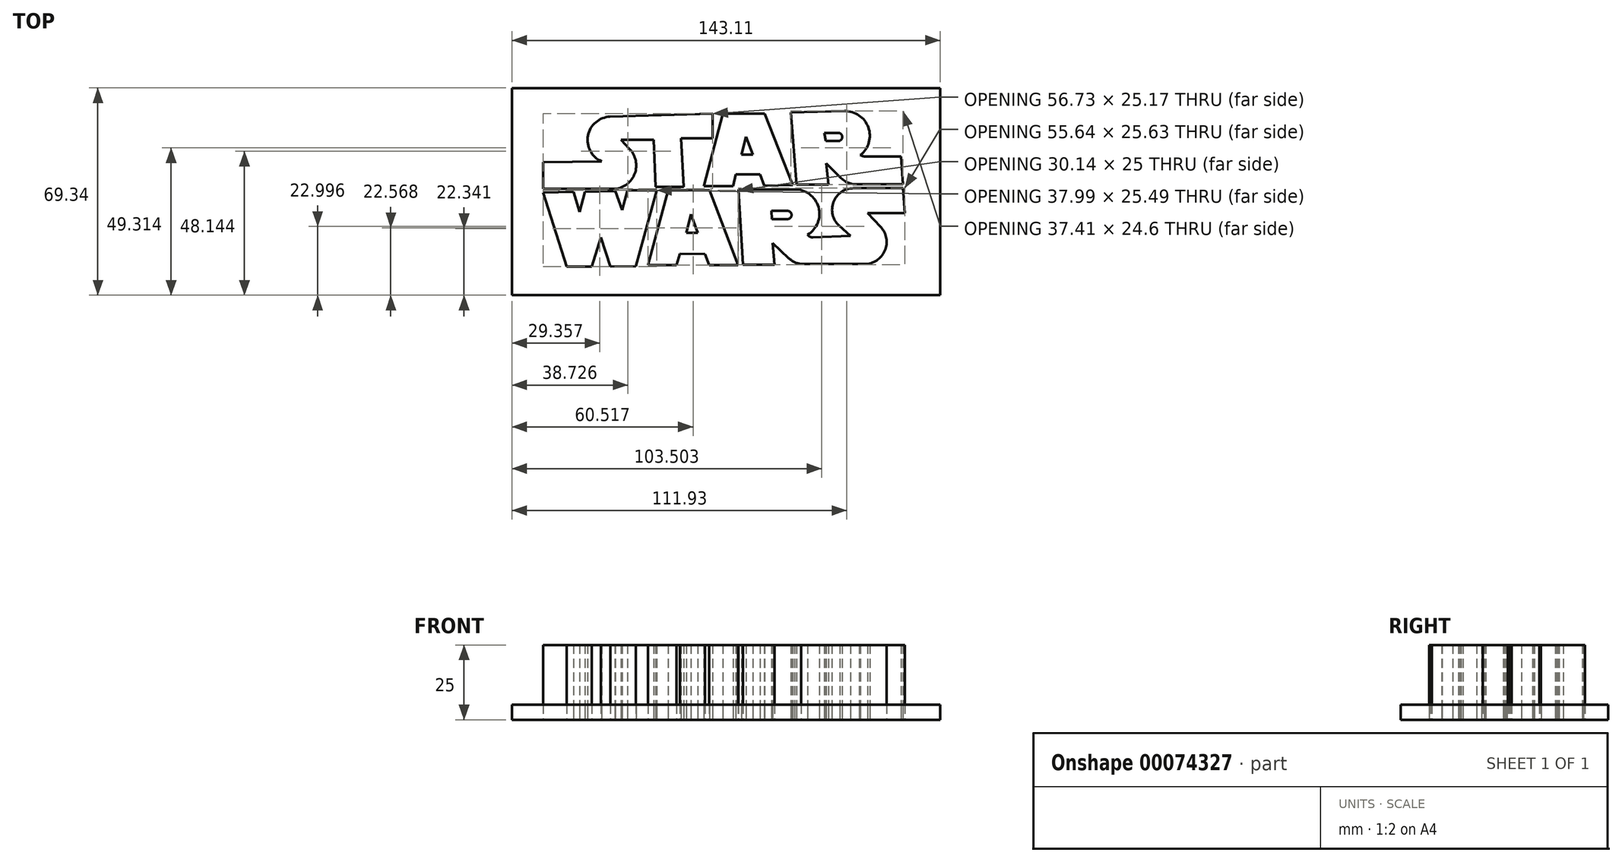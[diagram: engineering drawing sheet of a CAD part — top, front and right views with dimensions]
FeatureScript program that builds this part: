
annotation { "Feature Type Name" : "Feature", "Feature Type Description" : "" }
export const myFeature = defineFeature(function(context is Context, id is Id, definition is map)
    precondition{}
    {
        {
            var Q0;
            Q0=qCreatedBy(makeId("Top.planeOp"),FACE);
            var sketch = newSketch(context, id + "F0", { "sketchPlane" : qUnion([Q0])});
            skLineSegment(sketch, "E0", {"start": v(68.62, -36.54) * mm, "end": v(78.02, -36.54) * mm});
            skLineSegment(sketch, "E1", {"start": v(78.02, -36.54) * mm, "end": v(77.15, -20.37) * mm});
            skLineSegment(sketch, "E2", {"start": v(77.15, -20.37) * mm, "end": v(87.76, -20.37) * mm});
            skLineSegment(sketch, "E3", {"start": v(87.76, -20.37) * mm, "end": v(87.76, -12.11) * mm});
            skLineSegment(sketch, "E4", {"start": v(87.76, -12.11) * mm, "end": v(53.49, -13.1) * mm});
            skLineSegment(sketch, "E5", {"start": v(68.62, -36.54) * mm, "end": v(68.03, -20.87) * mm});
            skLineSegment(sketch, "E6", {"start": v(68.03, -20.87) * mm, "end": v(57.1, -20.87) * mm});
            skLineSegment(sketch, "E7", {"start": v(57.1, -20.87) * mm, "end": v(60.03, -23.97) * mm});
            skLineSegment(sketch, "E8", {"start": v(31.03, -28.3) * mm, "end": v(31.03, -37.28) * mm});
            skLineSegment(sketch, "E9", {"start": v(31.03, -37.28) * mm, "end": v(55.13, -37.28) * mm});
            skLineSegment(sketch, "E10", {"start": v(50.6, -28.05) * mm, "end": v(31.03, -28.3) * mm});
            skArc(sketch, "E11", {"start": v(53.49, -13.1) * mm, "mid": v(46.06, -19.42) * mm, "end": v(50.6, -28.05) * mm});
            skArc(sketch, "E12", {"start": v(55.13, -37.28) * mm, "mid": v(61.7, -32.14) * mm, "end": v(60.03, -23.97) * mm});
            skLineSegment(sketch, "E13", {"start": v(98.83, -19.8) * mm, "end": v(97.31, -25.8) * mm});
            skLineSegment(sketch, "E14", {"start": v(97.31, -25.8) * mm, "end": v(101.14, -25.8) * mm});
            skLineSegment(sketch, "E15", {"start": v(101.14, -25.8) * mm, "end": v(98.83, -19.8) * mm});
            skLineSegment(sketch, "E16", {"start": v(91.14, -12.01) * mm, "end": v(105.05, -12.01) * mm});
            skLineSegment(sketch, "E17", {"start": v(105.05, -12.01) * mm, "end": v(114.46, -35.91) * mm});
            skLineSegment(sketch, "E18", {"start": v(114.46, -35.91) * mm, "end": v(105.02, -36.2) * mm});
            skLineSegment(sketch, "E19", {"start": v(105.02, -36.2) * mm, "end": v(103.54, -32.45) * mm});
            skLineSegment(sketch, "E20", {"start": v(103.54, -32.45) * mm, "end": v(95.4, -32.45) * mm});
            skLineSegment(sketch, "E21", {"start": v(95.4, -32.45) * mm, "end": v(94.52, -36.4) * mm});
            skLineSegment(sketch, "E22", {"start": v(94.52, -36.4) * mm, "end": v(84.84, -36.4) * mm});
            skLineSegment(sketch, "E23", {"start": v(84.84, -36.4) * mm, "end": v(91.14, -12.01) * mm});
            skLineSegment(sketch, "E24.bottom", {"start": v(20.67, -3.5) * mm, "end": v(163.78, -3.5) * mm});
            skLineSegment(sketch, "E24.top", {"start": v(20.67, -72.84) * mm, "end": v(163.78, -72.84) * mm});
            skLineSegment(sketch, "E24.left", {"start": v(20.67, -3.5) * mm, "end": v(20.67, -72.84) * mm});
            skLineSegment(sketch, "E24.right", {"start": v(163.78, -3.5) * mm, "end": v(163.78, -72.84) * mm});
            skLineSegment(sketch, "E25", {"start": v(113.9, -11.65) * mm, "end": v(115.74, -35.83) * mm});
            skLineSegment(sketch, "E26", {"start": v(115.74, -35.83) * mm, "end": v(126.45, -35.83) * mm});
            skLineSegment(sketch, "E27", {"start": v(126.45, -35.83) * mm, "end": v(125.63, -28.76) * mm});
            skLineSegment(sketch, "E28", {"start": v(125.63, -28.76) * mm, "end": v(130.7, -33.69) * mm});
            skLineSegment(sketch, "E29", {"start": v(113.9, -11.65) * mm, "end": v(131.78, -11.23) * mm});
            skLineSegment(sketch, "E30", {"start": v(125.1, -18.49) * mm, "end": v(125.52, -21.17) * mm});
            skLineSegment(sketch, "E31", {"start": v(125.52, -21.17) * mm, "end": v(130.21, -21.17) * mm});
            skLineSegment(sketch, "E32", {"start": v(125.1, -18.49) * mm, "end": v(129.65, -18.49) * mm});
            skLineSegment(sketch, "E33", {"start": v(136.7, -35.68) * mm, "end": v(151.3, -35.68) * mm});
            skLineSegment(sketch, "E34", {"start": v(151.3, -35.68) * mm, "end": v(150.64, -26.43) * mm});
            skLineSegment(sketch, "E35", {"start": v(150.64, -26.43) * mm, "end": v(138.86, -26.43) * mm});
            skArc(sketch, "E36", {"start": v(130.7, -33.69) * mm, "mid": v(133.46, -35.37) * mm, "end": v(136.7, -35.68) * mm});
            skArc(sketch, "E37", {"start": v(137.16, -25.96) * mm, "mid": v(139.76, -16.66) * mm, "end": v(131.78, -11.23) * mm});
            skArc(sketch, "E38", {"start": v(137.16, -25.96) * mm, "mid": v(137.98, -26.3) * mm, "end": v(138.86, -26.43) * mm});
            skArc(sketch, "E39", {"start": v(130.21, -21.17) * mm, "mid": v(131.02, -19.6) * mm, "end": v(129.65, -18.49) * mm});
            skLineSegment(sketch, "E40", {"start": v(31.03, -38.52) * mm, "end": v(38.96, -63.2) * mm});
            skLineSegment(sketch, "E41", {"start": v(38.96, -63.2) * mm, "end": v(47.3, -63.2) * mm});
            skLineSegment(sketch, "E42", {"start": v(47.3, -63.2) * mm, "end": v(50.33, -53.49) * mm});
            skLineSegment(sketch, "E43", {"start": v(50.33, -53.49) * mm, "end": v(53.51, -63.24) * mm});
            skLineSegment(sketch, "E44", {"start": v(53.51, -63.24) * mm, "end": v(62.03, -63.09) * mm});
            skLineSegment(sketch, "E45", {"start": v(62.03, -63.09) * mm, "end": v(69.02, -37.76) * mm});
            skLineSegment(sketch, "E46", {"start": v(69.02, -37.76) * mm, "end": v(59.22, -37.76) * mm});
            skLineSegment(sketch, "E47", {"start": v(59.22, -37.76) * mm, "end": v(57.43, -44.37) * mm});
            skLineSegment(sketch, "E48", {"start": v(57.43, -44.37) * mm, "end": v(55.2, -37.98) * mm});
            skLineSegment(sketch, "E49", {"start": v(55.2, -37.98) * mm, "end": v(44.98, -38.18) * mm});
            skLineSegment(sketch, "E50", {"start": v(44.98, -38.18) * mm, "end": v(43.26, -44.9) * mm});
            skLineSegment(sketch, "E51", {"start": v(43.26, -44.9) * mm, "end": v(41.28, -38.29) * mm});
            skLineSegment(sketch, "E52", {"start": v(41.28, -38.29) * mm, "end": v(31.03, -38.52) * mm});
            skLineSegment(sketch, "E53", {"start": v(66.12, -62.77) * mm, "end": v(75.72, -62.77) * mm});
            skLineSegment(sketch, "E54", {"start": v(75.72, -62.77) * mm, "end": v(76.78, -58.98) * mm});
            skLineSegment(sketch, "E55", {"start": v(76.78, -58.98) * mm, "end": v(85.13, -59.05) * mm});
            skLineSegment(sketch, "E56", {"start": v(85.13, -59.05) * mm, "end": v(86.55, -62.73) * mm});
            skLineSegment(sketch, "E57", {"start": v(86.55, -62.73) * mm, "end": v(96.26, -62.74) * mm});
            skLineSegment(sketch, "E58", {"start": v(96.26, -62.74) * mm, "end": v(86.7, -37.77) * mm});
            skLineSegment(sketch, "E59", {"start": v(86.7, -37.77) * mm, "end": v(72.85, -37.77) * mm});
            skLineSegment(sketch, "E60", {"start": v(72.85, -37.77) * mm, "end": v(66.12, -62.77) * mm});
            skLineSegment(sketch, "E61", {"start": v(80.48, -45.71) * mm, "end": v(78.9, -51.96) * mm});
            skLineSegment(sketch, "E62", {"start": v(78.9, -51.96) * mm, "end": v(82.75, -51.96) * mm});
            skLineSegment(sketch, "E63", {"start": v(82.75, -51.96) * mm, "end": v(80.48, -45.71) * mm});
            skLineSegment(sketch, "E64", {"start": v(96.36, -37.45) * mm, "end": v(97.81, -62.66) * mm});
            skLineSegment(sketch, "E65", {"start": v(97.81, -62.66) * mm, "end": v(108.41, -62.66) * mm});
            skLineSegment(sketch, "E66", {"start": v(107.84, -55.43) * mm, "end": v(108.41, -62.66) * mm});
            skLineSegment(sketch, "E67", {"start": v(107.84, -55.43) * mm, "end": v(113.17, -60.43) * mm});
            skArc(sketch, "E68", {"start": v(113.17, -60.43) * mm, "mid": v(115.06, -61.73) * mm, "end": v(117.25, -62.41) * mm});
            skLineSegment(sketch, "E69", {"start": v(117.25, -62.41) * mm, "end": v(138.48, -62.41) * mm});
            skArc(sketch, "E70", {"start": v(138.48, -62.41) * mm, "mid": v(145.28, -57.94) * mm, "end": v(143.85, -49.93) * mm});
            skLineSegment(sketch, "E71", {"start": v(143.85, -49.93) * mm, "end": v(139.53, -45.38) * mm});
            skLineSegment(sketch, "E72", {"start": v(139.53, -45.38) * mm, "end": v(152, -45.38) * mm});
            skLineSegment(sketch, "E73", {"start": v(152, -45.38) * mm, "end": v(151.37, -37.03) * mm});
            skLineSegment(sketch, "E74", {"start": v(151.37, -37.03) * mm, "end": v(134.84, -37.03) * mm});
            skArc(sketch, "E75", {"start": v(134.84, -37.03) * mm, "mid": v(128.12, -41.66) * mm, "end": v(130.06, -49.6) * mm});
            skLineSegment(sketch, "E76", {"start": v(130.06, -49.6) * mm, "end": v(133.8, -52.93) * mm});
            skLineSegment(sketch, "E77", {"start": v(133.8, -52.93) * mm, "end": v(121.2, -53.48) * mm});
            skArc(sketch, "E78", {"start": v(119.48, -52.6) * mm, "mid": v(120.22, -53.27) * mm, "end": v(121.2, -53.48) * mm});
            skArc(sketch, "E79", {"start": v(119.48, -52.6) * mm, "mid": v(123.11, -43.37) * mm, "end": v(115.15, -37.43) * mm});
            skLineSegment(sketch, "E80", {"start": v(115.15, -37.43) * mm, "end": v(96.36, -37.45) * mm});
            skLineSegment(sketch, "E81", {"start": v(107.37, -44.62) * mm, "end": v(107.53, -47.35) * mm});
            skLineSegment(sketch, "E82", {"start": v(107.53, -47.35) * mm, "end": v(112.73, -47.35) * mm});
            skLineSegment(sketch, "E83", {"start": v(107.37, -44.62) * mm, "end": v(112.73, -44.62) * mm});
            skArc(sketch, "E84", {"start": v(112.73, -47.35) * mm, "mid": v(114.1, -45.98) * mm, "end": v(112.73, -44.62) * mm});
            skSolve(sketch);
        }
        {
            var Q0;
            Q0=makeQuery(id+"F0.imprint","IMPRINT",FACE,{"disambiguationData":[TD([[makeQuery(id+"F0.imprint","IMPRINT",EDGE,{"derivedFrom":sQuery(id+"F0.wireOp",EDGE,"E0")}),1.0]])]});
            var Q1;
            Q1=makeQuery(id+"F0.imprint","IMPRINT",FACE,{"disambiguationData":[TD([[makeQuery(id+"F0.imprint","IMPRINT",EDGE,{"derivedFrom":sQuery(id+"F0.wireOp",EDGE,"E13")}),-1.0]])]});
            var Q2;
            Q2=makeQuery(id+"F0.imprint","IMPRINT",FACE,{"disambiguationData":[TD([[makeQuery(id+"F0.imprint","IMPRINT",EDGE,{"derivedFrom":sQuery(id+"F0.wireOp",EDGE,"E25")}),1.0]])]});
            var Q3;
            Q3=makeQuery(id+"F0.imprint","IMPRINT",FACE,{"disambiguationData":[TD([[makeQuery(id+"F0.imprint","IMPRINT",EDGE,{"derivedFrom":sQuery(id+"F0.wireOp",EDGE,"E40")}),1.0]])]});
            var Q4;
            Q4=makeQuery(id+"F0.imprint","IMPRINT",FACE,{"disambiguationData":[TD([[makeQuery(id+"F0.imprint","IMPRINT",EDGE,{"derivedFrom":sQuery(id+"F0.wireOp",EDGE,"E53")}),1.0]])]});
            var Q5;
            Q5=makeQuery(id+"F0.imprint","IMPRINT",FACE,{"disambiguationData":[TD([[makeQuery(id+"F0.imprint","IMPRINT",EDGE,{"derivedFrom":sQuery(id+"F0.wireOp",EDGE,"E64")}),1.0]])]});
            extrude(context, id + "F1", {"entities" : qUnion([Q0, Q1, Q2, Q3, Q4, Q5]), "depth" : 25 * mm});
        }
        {
            var Q0;
            Q0=makeQuery(id+"F0.imprint","IMPRINT",FACE,{"disambiguationData":[TD([[makeQuery(id+"F0.imprint","IMPRINT",EDGE,{"derivedFrom":sQuery(id+"F0.wireOp",EDGE,"E0")}),-1.0]])]});
            var Q1;
            Q1=makeQuery(id+"F0.imprint","IMPRINT",FACE,{"disambiguationData":[TD([[makeQuery(id+"F0.imprint","IMPRINT",EDGE,{"derivedFrom":sQuery(id+"F0.wireOp",EDGE,"E13")}),1.0]])]});
            var Q2;
            Q2=makeQuery(id+"F0.imprint","IMPRINT",FACE,{"disambiguationData":[TD([[makeQuery(id+"F0.imprint","IMPRINT",EDGE,{"derivedFrom":sQuery(id+"F0.wireOp",EDGE,"E30")}),1.0]])]});
            var Q3;
            Q3=makeQuery(id+"F0.imprint","IMPRINT",FACE,{"disambiguationData":[TD([[makeQuery(id+"F0.imprint","IMPRINT",EDGE,{"derivedFrom":sQuery(id+"F0.wireOp",EDGE,"E81")}),1.0]])]});
            var Q4;
            Q4=makeQuery(id+"F0.imprint","IMPRINT",FACE,{"disambiguationData":[TD([[makeQuery(id+"F0.imprint","IMPRINT",EDGE,{"derivedFrom":sQuery(id+"F0.wireOp",EDGE,"E61")}),1.0]])]});
            extrude(context, id + "F2", {"entities" : qUnion([Q0, Q1, Q2, Q3, Q4]), "depth" : 5 * mm});
        }
    });
